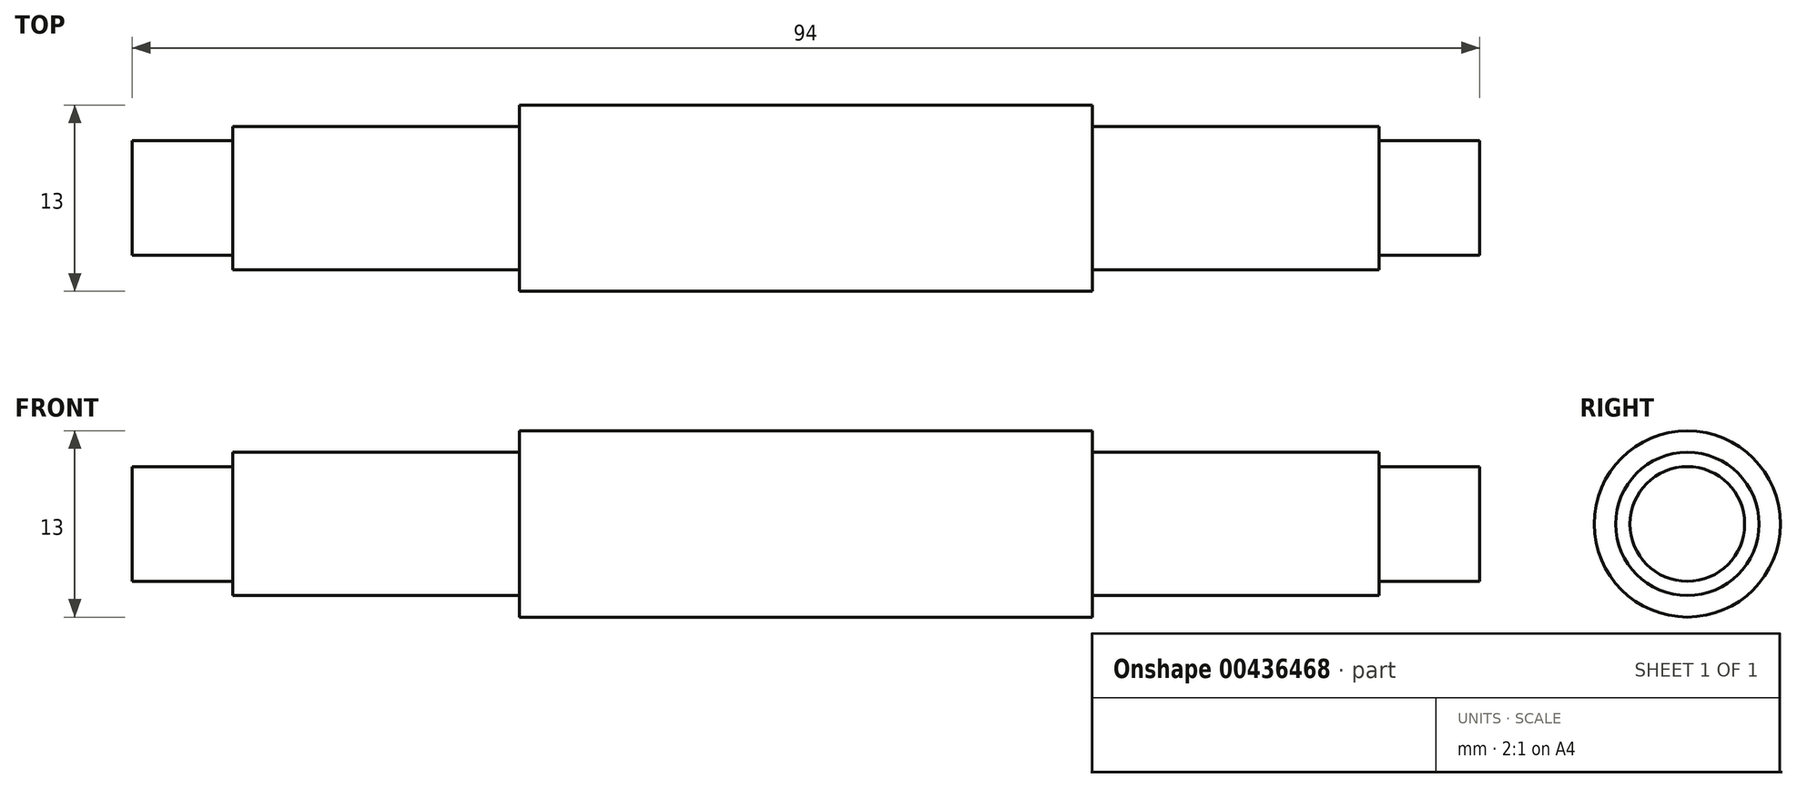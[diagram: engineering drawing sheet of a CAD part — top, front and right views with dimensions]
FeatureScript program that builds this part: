
annotation { "Feature Type Name" : "Feature", "Feature Type Description" : "" }
export const myFeature = defineFeature(function(context is Context, id is Id, definition is map)
    precondition{}
    {
        {
            var Q0;
            Q0=qCreatedBy(makeId("Front.planeOp"),FACE);
            var sketch = newSketch(context, id + "F0", { "sketchPlane" : qUnion([Q0])});
            skLineSegment(sketch, "E0", {"start": v(-47, 0) * mm, "end": v(-47, 4) * mm});
            skLineSegment(sketch, "E1", {"start": v(-47, 4) * mm, "end": v(-40, 4) * mm});
            skLineSegment(sketch, "E2", {"start": v(-40, 4) * mm, "end": v(-40, 5) * mm});
            skLineSegment(sketch, "E3", {"start": v(-40, 5) * mm, "end": v(-20, 5) * mm});
            skLineSegment(sketch, "E4", {"start": v(-20, 5) * mm, "end": v(-20, 6.5) * mm});
            skLineSegment(sketch, "E5", {"start": v(-20, 6.5) * mm, "end": v(20, 6.5) * mm});
            skLineSegment(sketch, "E6", {"start": v(20, 6.5) * mm, "end": v(20, 5) * mm});
            skLineSegment(sketch, "E7", {"start": v(20, 5) * mm, "end": v(40, 5) * mm});
            skLineSegment(sketch, "E8", {"start": v(40, 5) * mm, "end": v(40, 4) * mm});
            skLineSegment(sketch, "E9", {"start": v(40, 4) * mm, "end": v(47, 4) * mm});
            skLineSegment(sketch, "E10", {"start": v(47, 4) * mm, "end": v(47, 0) * mm});
            skLineSegment(sketch, "E11", {"start": v(47, 0) * mm, "end": v(-47, 0) * mm});
            skSolve(sketch);
        }
        {
            var Q0;
            Q0 = qSketchRegion(id + "F0", true);
            var Q1;
            Q1=sQuery(id+"F0.wireOp",EDGE,"E11");
            revolve(context, id + "F1", {"entities" : qUnion([Q0]), "axis" : qUnion([Q1]), "revolveType" : RevolveType.FULL});
        }
    });
